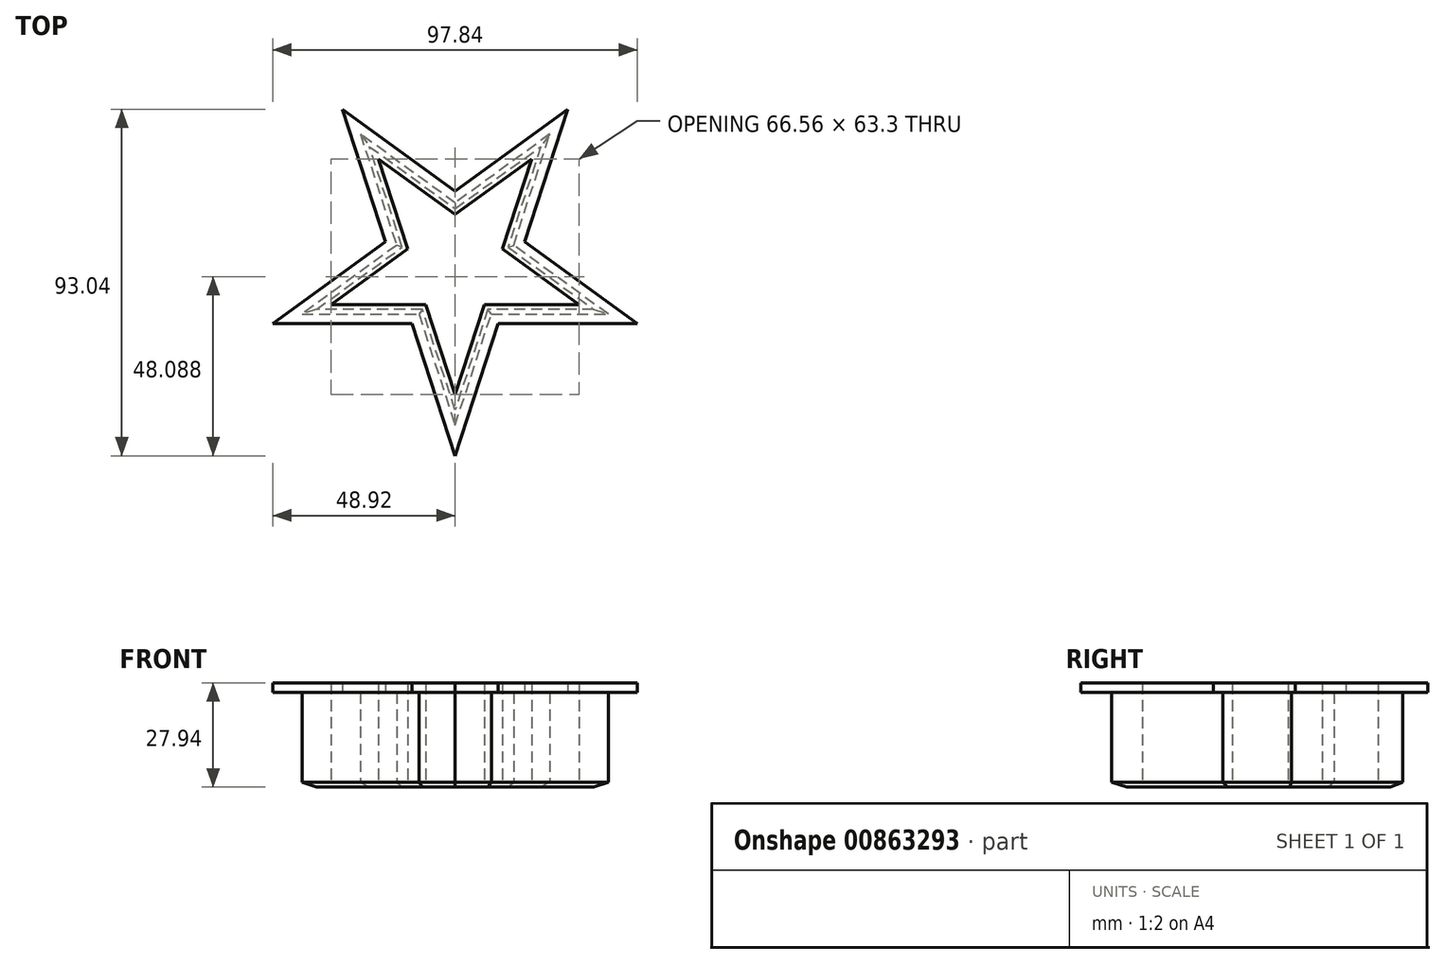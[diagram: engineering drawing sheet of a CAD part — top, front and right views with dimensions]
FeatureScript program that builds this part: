
annotation { "Feature Type Name" : "Feature", "Feature Type Description" : "" }
export const myFeature = defineFeature(function(context is Context, id is Id, definition is map)
    precondition{}
    {
        {
            var Q0;
            Q0=qCreatedBy(makeId("Top.planeOp"),FACE);
            var sketch = newSketch(context, id + "F0", { "sketchPlane" : qUnion([Q0])});
            skLineSegment(sketch, "E0", {"start": v(-25.4, 34.96) * mm, "end": v(-15.7, 5.1) * mm});
            skLineSegment(sketch, "E1", {"start": v(25.4, 34.96) * mm, "end": v(15.7, 5.1) * mm});
            skLineSegment(sketch, "E2", {"start": v(25.4, 34.96) * mm, "end": v(0, 16.5) * mm});
            skLineSegment(sketch, "E3", {"start": v(-41.1, -13.35) * mm, "end": v(-9.7, -13.35) * mm});
            skLineSegment(sketch, "E4", {"start": v(-25.4, 34.96) * mm, "end": v(0, 16.5) * mm});
            skLineSegment(sketch, "E5.trimOffspring", {"start": v(-15.7, 5.1) * mm, "end": v(-41.1, -13.35) * mm});
            skLineSegment(sketch, "E6.trimOffspring", {"start": v(15.7, 5.1) * mm, "end": v(41.1, -13.35) * mm});
            skLineSegment(sketch, "E7.trimOffspring", {"start": v(9.7, -13.35) * mm, "end": v(0, -43.21) * mm});
            skLineSegment(sketch, "E8.trimOffspring", {"start": v(9.7, -13.35) * mm, "end": v(41.1, -13.35) * mm});
            skLineSegment(sketch, "E9.trimOffspring", {"start": v(-9.7, -13.35) * mm, "end": v(0, -43.21) * mm});
            skPoint(sketch, "E10.cCircle.center.orphan", {"position": v(0, 0) * mm});
            skLineSegment(sketch, "E11.0", {"start": v(-20.57, 28.31) * mm, "end": v(-12.71, 4.13) * mm});
            skLineSegment(sketch, "E11.1", {"start": v(-12.71, 4.13) * mm, "end": v(-33.28, -10.81) * mm});
            skLineSegment(sketch, "E11.2", {"start": v(-20.57, 28.31) * mm, "end": v(0, 13.37) * mm});
            skLineSegment(sketch, "E11.3", {"start": v(-33.28, -10.81) * mm, "end": v(-7.86, -10.81) * mm});
            skLineSegment(sketch, "E11.4", {"start": v(-7.86, -10.81) * mm, "end": v(0, -35) * mm});
            skLineSegment(sketch, "E11.5", {"start": v(7.86, -10.81) * mm, "end": v(0, -35) * mm});
            skLineSegment(sketch, "E11.6", {"start": v(20.57, 28.31) * mm, "end": v(0, 13.37) * mm});
            skLineSegment(sketch, "E11.7", {"start": v(20.57, 28.31) * mm, "end": v(12.71, 4.13) * mm});
            skLineSegment(sketch, "E11.8", {"start": v(12.71, 4.13) * mm, "end": v(33.28, -10.81) * mm});
            skLineSegment(sketch, "E11.9", {"start": v(7.86, -10.81) * mm, "end": v(33.28, -10.81) * mm});
            skSolve(sketch);
        }
        {
            var Q0;
            Q0=makeQuery(id+"F0.imprint","IMPRINT",FACE,{"disambiguationData":[TD([[makeQuery(id+"F0.imprint","IMPRINT",EDGE,{"derivedFrom":sQuery(id+"F0.wireOp",EDGE,"E0")}),1.0]])]});
            extrude(context, id + "F1", {"entities" : qUnion([Q0]), "depth" : 25.4 * mm, "offsetDistance" : 25.4 * mm});
        }
        {
            var Q0;
            Q0=makeQuery(id+"F1.opExtrude","CAP_FACE",FACE,{"disambiguationData":[OSD([sQuery(id+"F0.wireOp",EDGE,"E0"),sQuery(id+"F0.wireOp",EDGE,"E1"),sQuery(id+"F0.wireOp",EDGE,"E2"),sQuery(id+"F0.wireOp",EDGE,"E3"),sQuery(id+"F0.wireOp",EDGE,"E4"),sQuery(id+"F0.wireOp",EDGE,"E5.trimOffspring"),sQuery(id+"F0.wireOp",EDGE,"E6.trimOffspring"),sQuery(id+"F0.wireOp",EDGE,"E7.trimOffspring"),sQuery(id+"F0.wireOp",EDGE,"E8.trimOffspring"),sQuery(id+"F0.wireOp",EDGE,"E9.trimOffspring"),sQuery(id+"F0.wireOp",EDGE,"E11.0"),sQuery(id+"F0.wireOp",EDGE,"E11.1"),sQuery(id+"F0.wireOp",EDGE,"E11.2"),sQuery(id+"F0.wireOp",EDGE,"E11.3"),sQuery(id+"F0.wireOp",EDGE,"E11.4"),sQuery(id+"F0.wireOp",EDGE,"E11.5"),sQuery(id+"F0.wireOp",EDGE,"E11.6"),sQuery(id+"F0.wireOp",EDGE,"E11.7"),sQuery(id+"F0.wireOp",EDGE,"E11.8"),sQuery(id+"F0.wireOp",EDGE,"E11.9")])],"isStart":false});
            var sketch = newSketch(context, id + "F2", { "sketchPlane" : qUnion([Q0])});
            skLineSegment(sketch, "E12.0", {"start": v(30.23, 41.6) * mm, "end": v(18.68, 6.07) * mm});
            skLineSegment(sketch, "E12.1", {"start": v(30.23, 41.6) * mm, "end": v(0, 19.65) * mm});
            skLineSegment(sketch, "E12.2", {"start": v(18.68, 6.07) * mm, "end": v(48.92, -15.9) * mm});
            skLineSegment(sketch, "E12.3", {"start": v(-30.23, 41.6) * mm, "end": v(0, 19.65) * mm});
            skLineSegment(sketch, "E12.4", {"start": v(-30.23, 41.6) * mm, "end": v(-18.68, 6.07) * mm});
            skLineSegment(sketch, "E12.5", {"start": v(-18.68, 6.07) * mm, "end": v(-48.92, -15.9) * mm});
            skLineSegment(sketch, "E12.6", {"start": v(11.55, -15.9) * mm, "end": v(48.92, -15.9) * mm});
            skLineSegment(sketch, "E12.7", {"start": v(11.55, -15.9) * mm, "end": v(0, -51.43) * mm});
            skLineSegment(sketch, "E12.8", {"start": v(-11.55, -15.9) * mm, "end": v(0, -51.43) * mm});
            skLineSegment(sketch, "E12.9", {"start": v(-48.92, -15.9) * mm, "end": v(-11.55, -15.9) * mm});
            skSolve(sketch);
        }
        {
            var Q0;
            Q0=makeQuery(id+"F2.imprint","IMPRINT",FACE,{"disambiguationData":[TD([[makeQuery(id+"F2.imprint","IMPRINT",EDGE,{"derivedFrom":sQuery(id+"F2.wireOp",EDGE,"E12.0")}),-1.0]])]});
            var Q1;
            Q1=makeQuery(id+"F2.imprint","IMPRINT",FACE,{"disambiguationData":[TD([[makeQuery(id+"F2.imprint","IMPRINT",EDGE,{"derivedFrom":makeQuery(id+"F1.opExtrude","CAP_EDGE",EDGE,{"disambiguationData":[OSD([sQuery(id+"F0.wireOp",EDGE,"E0")])],"isStart":false})}),1.0]])]});
            extrude(context, id + "F3", {"entities" : qUnion([Q0, Q1]), "operationType" : NewBodyOperationType.ADD, "depth" : 2.54 * mm, "offsetDistance" : 25.4 * mm});
        }
        {
            var Q0;
            Q0=makeQuery(id+"F1.opExtrude","CAP_EDGE",EDGE,{"disambiguationData":[OSD([sQuery(id+"F0.wireOp",EDGE,"E1")])],"isStart":true});
            var Q1;
            Q1=makeQuery(id+"F1.opExtrude","CAP_EDGE",EDGE,{"disambiguationData":[OSD([sQuery(id+"F0.wireOp",EDGE,"E2")])],"isStart":true});
            var Q2;
            Q2=makeQuery(id+"F1.opExtrude","CAP_EDGE",EDGE,{"disambiguationData":[OSD([sQuery(id+"F0.wireOp",EDGE,"E4")])],"isStart":true});
            var Q3;
            Q3=makeQuery(id+"F1.opExtrude","CAP_EDGE",EDGE,{"disambiguationData":[OSD([sQuery(id+"F0.wireOp",EDGE,"E0")])],"isStart":true});
            var Q4;
            Q4=makeQuery(id+"F1.opExtrude","CAP_EDGE",EDGE,{"disambiguationData":[OSD([sQuery(id+"F0.wireOp",EDGE,"E5.trimOffspring")])],"isStart":true});
            var Q5;
            Q5=makeQuery(id+"F1.opExtrude","CAP_EDGE",EDGE,{"disambiguationData":[OSD([sQuery(id+"F0.wireOp",EDGE,"E3")])],"isStart":true});
            var Q6;
            Q6=makeQuery(id+"F1.opExtrude","CAP_EDGE",EDGE,{"disambiguationData":[OSD([sQuery(id+"F0.wireOp",EDGE,"E9.trimOffspring")])],"isStart":true});
            var Q7;
            Q7=makeQuery(id+"F1.opExtrude","CAP_EDGE",EDGE,{"disambiguationData":[OSD([sQuery(id+"F0.wireOp",EDGE,"E7.trimOffspring")])],"isStart":true});
            var Q8;
            Q8=makeQuery(id+"F1.opExtrude","CAP_EDGE",EDGE,{"disambiguationData":[OSD([sQuery(id+"F0.wireOp",EDGE,"E8.trimOffspring")])],"isStart":true});
            var Q9;
            Q9=makeQuery(id+"F1.opExtrude","CAP_EDGE",EDGE,{"disambiguationData":[OSD([sQuery(id+"F0.wireOp",EDGE,"E6.trimOffspring")])],"isStart":true});
            chamfer(context, id + "F4", {"entities" : qUnion([Q0, Q1, Q2, Q3, Q4, Q5, Q6, Q7, Q8, Q9]), "width" : 1.27 * mm, "tangentPropagation" : true});
        }
    });
